# Revit family: PRD_AR_JntrlSnks_SIRIUSBoot-cleaningUnit_SIRB711
name_source: partatom
category: Plumbing Fixtures
revit_build: Autodesk Revit 2018 (Build: 20190510_1515(x64)
units: mm (PartAtom-declared; Revit-internal decimal feet)

## family parameters
Cut with Voids When Loaded = Yes
Host = Face
OmniClass Number = 23.45.05.14.14.27
OmniClass Title = Service Sinks
Part Type = Normal
Room Calculation Point = No
Round Connector Dimension = Use Diameter
Shared = Yes

## types (1)
- SIRB711
    AssetType = Fixed
    BIMObjectName = PRD_AR_JanitorialSinks_SIRIUSBoot-cleaningUnit_SIRB711
    BowlFinish = High polished
    Brushes = Hand and sole brushes
    Category = Pr_40_20_96_44, Janitorial sinks
    Color = anthracite
    Default Elevation = 0 mm  [stored 0 ft]
    Description = Boot cleaning unit made of resin-bonded mineral material with smooth, pore-free surface, anthracite colour. With height-adjustable feet, galvanized folding grid, manual brush with lever valve, grab handle, sole-cleaning brushes, spray arrays and DN 15 foot valve.
    DiameterNominal = 15  [stored 0.0492126 ft]
    DrainSize = 100 mm  [stored 0.328084 ft]
    DrainerOrStorage = No
    DurationUnit = year
    Features = Without feet, with DN 100 waste outlet spigot, horizontal. Dimensions 600 x 205 x 900 mm (W x H x D)
    Finish = smooth, pore-free
    Grid = Hinged
    GrossWeight = 38.00 kg
    IfcExportAs = IfcSanitaryTerminalType
    IfcExportType = SINK
    InletSize = G 1/2 B
    Manufacturer = KWC Group AG
    ManufacturerName = KWC Group AG
    ManufacturerURL = www.kwc.com
    Material = Mineral material
    MaterialCode = Miranit
    Model = SIRB711
    ModelNumber = 2000101085
    ModelReference = SIRB711
    Mounting = CounterTop
    MountingOffset = 0 mm  [stored 0 ft]
    NBSDescription = Janitorial units
    NBSReference = 45-35-70/401
    Name = SIRIUS Boot-cleaning unit SIRB711
    NetWeight = 36.10 kg
    NominalDepth = 900 mm  [stored 2.95276 ft]
    NominalHeight = 1095 mm  [stored 3.59252 ft]
    NominalWidth = 600 mm
    NumberOfBrushes = 1
    NumberOfWashPlaces = 1
    NumberOfWasteHoles = 1
    OutletSize = DN 100
    Overflow = No
    ProductCode = 207.0638.410
    ProductInformation = https://pim.kwc.com
    RearUpstand = No
    SinkType = USERDEFINED
    Size = 600 x 1095 x 900 mm (W x H x D)
    Spillway = No
    Splashback = No
    Sump = No
    SumpBasket = No
    TapLedge = No
    TypeOfMounting = Inset floor mounting
    TypeOfUtilitySink = Cleaner sink
    URL = www.kwc.com
    Uniclass2015Code = Pr_40_20_96_44
    Uniclass2015Title = Janitorial sinks
    Uniclass2015Version = Products v1.23
    Version = 1
    WarrantyDurationUnit = year
    WashRiffle = No
    WasteHolePosition = Center

note: [stored X ft] marks values corroborated as IEEE doubles in the binary element streams (Revit-internal decimal feet)

## geometry (parser evidence)
native form markers: Sweep x8
no freeform markers — native parametric forms only
